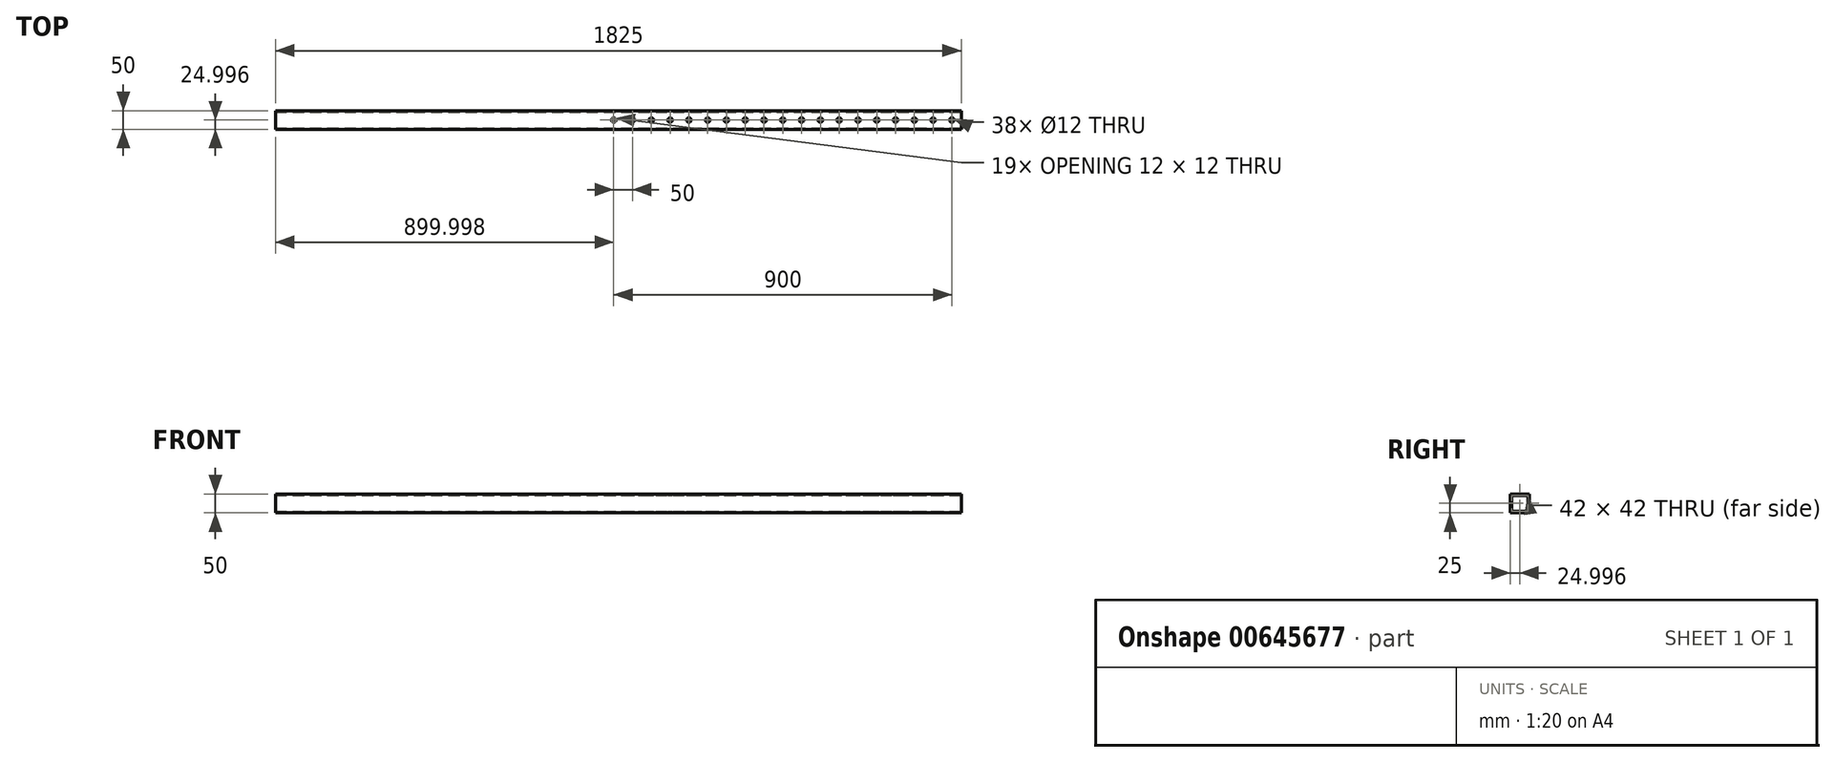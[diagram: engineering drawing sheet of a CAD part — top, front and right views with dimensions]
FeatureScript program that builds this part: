
annotation { "Feature Type Name" : "Feature", "Feature Type Description" : "" }
export const myFeature = defineFeature(function(context is Context, id is Id, definition is map)
    precondition{}
    {
        {
            var Q0;
            Q0=qCreatedBy(makeId("Top.planeOp"),FACE);
            var sketch = newSketch(context, id + "F0", { "sketchPlane" : qUnion([Q0])});
            skLineSegment(sketch, "E0.bottom", {"start": v(-23.46, 1747.64) * mm, "end": v(-23.46, 1797.64) * mm});
            skLineSegment(sketch, "E0.top", {"start": v(1801.54, 1747.64) * mm, "end": v(1801.54, 1797.64) * mm});
            skLineSegment(sketch, "E0.left", {"start": v(-23.46, 1747.64) * mm, "end": v(1801.54, 1747.64) * mm});
            skLineSegment(sketch, "E0.right", {"start": v(-23.46, 1797.64) * mm, "end": v(1801.54, 1797.64) * mm});
            skPoint(sketch, "E1.middle", {"position": v(-23.46, 1747.64) * mm});
            skPoint(sketch, "E2.middle", {"position": v(1.54, 3.58) * mm});
            skCircle(sketch, "E3", {"center": v(1776.54, 1772.64) * mm, "radius": 6 * mm});
            skCircle(sketch, "E4", {"center": v(876.54, 1772.64) * mm, "radius": 6 * mm});
            skCircle(sketch, "E5", {"center": v(1726.54, 1772.64) * mm, "radius": 6 * mm});
            skLineSegment(sketch, "E6", {"start": v(1801.54, 1772.64) * mm, "end": v(-23.46, 1772.64) * mm, "construction": true});
            skCircle(sketch, "E7", {"center": v(1526.54, 1772.64) * mm, "radius": 6 * mm});
            skCircle(sketch, "E8", {"center": v(1476.54, 1772.64) * mm, "radius": 6 * mm});
            skCircle(sketch, "E9", {"center": v(1426.54, 1772.64) * mm, "radius": 6 * mm});
            skCircle(sketch, "E10", {"center": v(1376.54, 1772.64) * mm, "radius": 6 * mm});
            skCircle(sketch, "E11", {"center": v(1326.54, 1772.64) * mm, "radius": 6 * mm});
            skCircle(sketch, "E12", {"center": v(1676.54, 1772.64) * mm, "radius": 6 * mm});
            skCircle(sketch, "E13", {"center": v(1626.54, 1772.64) * mm, "radius": 6 * mm});
            skCircle(sketch, "E14", {"center": v(1576.54, 1772.64) * mm, "radius": 6 * mm});
            skCircle(sketch, "E15", {"center": v(1276.54, 1772.64) * mm, "radius": 6 * mm});
            skCircle(sketch, "E16", {"center": v(1226.54, 1772.64) * mm, "radius": 6 * mm});
            skCircle(sketch, "E17", {"center": v(1176.54, 1772.64) * mm, "radius": 6 * mm});
            skCircle(sketch, "E18", {"center": v(1126.54, 1772.64) * mm, "radius": 6 * mm});
            skCircle(sketch, "E19", {"center": v(1076.54, 1772.64) * mm, "radius": 6 * mm});
            skCircle(sketch, "E20", {"center": v(1026.54, 1772.64) * mm, "radius": 6 * mm});
            skCircle(sketch, "E21", {"center": v(976.54, 1772.64) * mm, "radius": 6 * mm});
            skCircle(sketch, "E22", {"center": v(926.54, 1772.64) * mm, "radius": 6 * mm});
            skSolve(sketch);
        }
        {
            var Q0;
            Q0=makeQuery(id+"F0.imprint","IMPRINT",FACE,{"disambiguationData":[TD([[makeQuery(id+"F0.imprint","IMPRINT",EDGE,{"derivedFrom":sQuery(id+"F0.wireOp",EDGE,"E0.bottom")}),-1.0]])]});
            extrude(context, id + "F1", {"entities" : qUnion([Q0]), "depth" : 50 * mm, "offsetDistance" : 25 * mm});
        }
        {
            var Q0;
            Q0=makeQuery(id+"F1.opExtrude","SWEPT_FACE",FACE,{"disambiguationData":[OSD([sQuery(id+"F0.wireOp",EDGE,"E0.top")])]});
            var sketch = newSketch(context, id + "F2", { "sketchPlane" : qUnion([Q0])});
            skLineSegment(sketch, "E23.bottom", {"start": v(1751.64, 4) * mm, "end": v(1793.64, 4) * mm});
            skLineSegment(sketch, "E23.top", {"start": v(1751.64, 46) * mm, "end": v(1793.64, 46) * mm});
            skLineSegment(sketch, "E23.left", {"start": v(1751.64, 4) * mm, "end": v(1751.64, 46) * mm});
            skLineSegment(sketch, "E23.right", {"start": v(1793.64, 4) * mm, "end": v(1793.64, 46) * mm});
            skSolve(sketch);
        }
        {
            var Q0;
            Q0=makeQuery(id+"F2.imprint","IMPRINT",FACE,{"disambiguationData":[TD([[makeQuery(id+"F2.imprint","IMPRINT",EDGE,{"derivedFrom":sQuery(id+"F2.wireOp",EDGE,"E23.bottom")}),1.0]])]});
            extrude(context, id + "F3", {"entities" : qUnion([Q0]), "operationType" : NewBodyOperationType.REMOVE, "endBound" : BoundingType.THROUGH_ALL, "oppositeDirection" : true, "depth" : 25 * mm, "offsetDistance" : 25 * mm});
        }
    });
